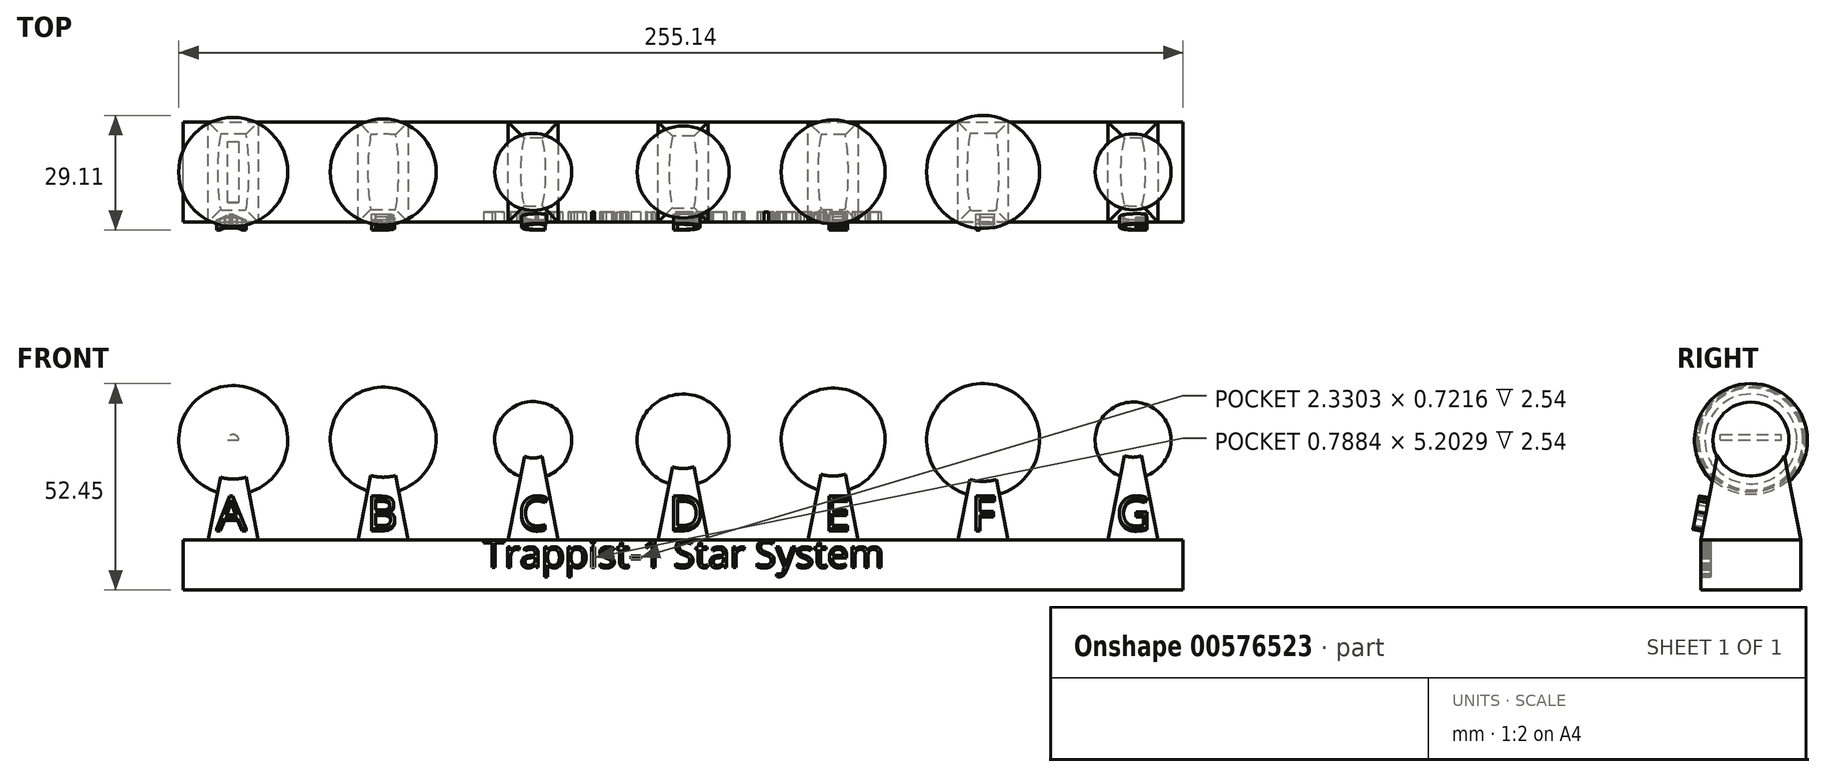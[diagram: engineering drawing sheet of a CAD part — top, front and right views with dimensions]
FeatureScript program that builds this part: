
annotation { "Feature Type Name" : "Feature", "Feature Type Description" : "" }
export const myFeature = defineFeature(function(context is Context, id is Id, definition is map)
    precondition{}
    {
        {
            var Q0;
            Q0=qCreatedBy(makeId("Front.planeOp"),FACE);
            var sketch = newSketch(context, id + "F0", { "sketchPlane" : qUnion([Q0])});
            skLineSegment(sketch, "E0.bottom", {"start": v(0, 0) * mm, "end": v(254, 0) * mm});
            skLineSegment(sketch, "E0.top", {"start": v(0, 12.7) * mm, "end": v(254, 12.7) * mm});
            skLineSegment(sketch, "E0.left", {"start": v(0, 0) * mm, "end": v(0, 12.7) * mm});
            skLineSegment(sketch, "E0.right", {"start": v(254, 0) * mm, "end": v(254, 12.7) * mm});
            skSolve(sketch);
        }
        {
            var Q0;
            Q0 = qSketchRegion(id + "F0", true);
            extrude(context, id + "F1", {"entities" : qUnion([Q0]), "depth" : 25.4 * mm, "offsetDistance" : 25.4 * mm});
        }
        {
            var Q0;
            Q0=makeQuery(id+"F1.opExtrude","SWEPT_FACE",FACE,{"disambiguationData":[OSD([sQuery(id+"F0.wireOp",EDGE,"E0.top")])]});
            var sketch = newSketch(context, id + "F2", { "sketchPlane" : qUnion([Q0])});
            skLineSegment(sketch, "E1.bottom", {"start": v(6.35, 0) * mm, "end": v(19.05, 0) * mm});
            skLineSegment(sketch, "E1.top", {"start": v(6.35, -25.4) * mm, "end": v(19.05, -25.4) * mm});
            skLineSegment(sketch, "E1.left", {"start": v(6.35, 0) * mm, "end": v(6.35, -25.4) * mm});
            skLineSegment(sketch, "E1.right", {"start": v(19.05, 0) * mm, "end": v(19.05, -25.4) * mm});
            skLineSegment(sketch, "E2.1.0.0", {"start": v(57.15, 0) * mm, "end": v(57.15, -25.4) * mm});
            skLineSegment(sketch, "E2.1.0.1", {"start": v(44.45, 0) * mm, "end": v(57.15, 0) * mm});
            skLineSegment(sketch, "E2.1.0.2", {"start": v(44.45, 0) * mm, "end": v(44.45, -25.4) * mm});
            skLineSegment(sketch, "E2.1.0.3", {"start": v(44.45, -25.4) * mm, "end": v(57.15, -25.4) * mm});
            skLineSegment(sketch, "E2.2.0.0", {"start": v(95.25, 0) * mm, "end": v(95.25, -25.4) * mm});
            skLineSegment(sketch, "E2.2.0.1", {"start": v(82.55, 0) * mm, "end": v(95.25, 0) * mm});
            skLineSegment(sketch, "E2.2.0.2", {"start": v(82.55, 0) * mm, "end": v(82.55, -25.4) * mm});
            skLineSegment(sketch, "E2.2.0.3", {"start": v(82.55, -25.4) * mm, "end": v(95.25, -25.4) * mm});
            skLineSegment(sketch, "E2.3.0.0", {"start": v(133.35, 0) * mm, "end": v(133.35, -25.4) * mm});
            skLineSegment(sketch, "E2.3.0.1", {"start": v(120.65, 0) * mm, "end": v(133.35, 0) * mm});
            skLineSegment(sketch, "E2.3.0.2", {"start": v(120.65, 0) * mm, "end": v(120.65, -25.4) * mm});
            skLineSegment(sketch, "E2.3.0.3", {"start": v(120.65, -25.4) * mm, "end": v(133.35, -25.4) * mm});
            skLineSegment(sketch, "E2.4.0.0", {"start": v(171.45, 0) * mm, "end": v(171.45, -25.4) * mm});
            skLineSegment(sketch, "E2.4.0.1", {"start": v(158.75, 0) * mm, "end": v(171.45, 0) * mm});
            skLineSegment(sketch, "E2.4.0.2", {"start": v(158.75, 0) * mm, "end": v(158.75, -25.4) * mm});
            skLineSegment(sketch, "E2.4.0.3", {"start": v(158.75, -25.4) * mm, "end": v(171.45, -25.4) * mm});
            skLineSegment(sketch, "E2.5.0.0", {"start": v(209.55, 0) * mm, "end": v(209.55, -25.4) * mm});
            skLineSegment(sketch, "E2.5.0.1", {"start": v(196.85, 0) * mm, "end": v(209.55, 0) * mm});
            skLineSegment(sketch, "E2.5.0.2", {"start": v(196.85, 0) * mm, "end": v(196.85, -25.4) * mm});
            skLineSegment(sketch, "E2.5.0.3", {"start": v(196.85, -25.4) * mm, "end": v(209.55, -25.4) * mm});
            skLineSegment(sketch, "E2.6.0.0", {"start": v(247.65, 0) * mm, "end": v(247.65, -25.4) * mm});
            skLineSegment(sketch, "E2.6.0.1", {"start": v(234.95, 0) * mm, "end": v(247.65, 0) * mm});
            skLineSegment(sketch, "E2.6.0.2", {"start": v(234.95, 0) * mm, "end": v(234.95, -25.4) * mm});
            skLineSegment(sketch, "E2.6.0.3", {"start": v(234.95, -25.4) * mm, "end": v(247.65, -25.4) * mm});
            skLineSegment(sketch, "E2.direction1", {"start": v(19.05, -25.4) * mm, "end": v(57.15, -25.4) * mm, "construction": true});
            skSolve(sketch);
        }
        {
            var Q0;
            Q0 = qSketchRegion(id + "F2", true);
            extrude(context, id + "F3", {"entities" : qUnion([Q0]), "operationType" : NewBodyOperationType.ADD, "depth" : 25.4 * mm, "offsetDistance" : 25.4 * mm, "hasDraft" : true, "draftAngle" : 11 * degree, "draftPullDirection" : true});
        }
        {
            var Q0;
            Q0=makeQuery(id+"F3.opExtrude","CAP_FACE",FACE,{"disambiguationData":[OSD([sQuery(id+"F2.wireOp",EDGE,"E1.bottom"),sQuery(id+"F2.wireOp",EDGE,"E1.top"),sQuery(id+"F2.wireOp",EDGE,"E1.left"),sQuery(id+"F2.wireOp",EDGE,"E1.right")])],"isStart":false});
            var sketch = newSketch(context, id + "F4", { "sketchPlane" : qUnion([Q0])});
            skLineSegment(sketch, "E3", {"start": v(12.7, -20.46) * mm, "end": v(12.7, -4.94) * mm});
            skLineSegment(sketch, "E4", {"start": v(12.7, -4.94) * mm, "end": v(12.7, 24.87) * mm});
            skLineSegment(sketch, "E5", {"start": v(12.7, 24.87) * mm, "end": v(12.7, -38.9) * mm});
            skCircle(sketch, "E6", {"center": v(12.7, -12.7) * mm, "radius": 13.84 * mm});
            skLineSegment(sketch, "E7", {"start": v(50.8, -20.46) * mm, "end": v(50.8, -4.94) * mm});
            skLineSegment(sketch, "E8.1.0.0", {"start": v(88.9, -20.46) * mm, "end": v(88.9, -4.94) * mm});
            skLineSegment(sketch, "E8.2.0.0", {"start": v(127, -20.46) * mm, "end": v(127, -4.94) * mm});
            skLineSegment(sketch, "E8.3.0.0", {"start": v(165.1, -20.46) * mm, "end": v(165.1, -4.94) * mm});
            skLineSegment(sketch, "E8.4.0.0", {"start": v(203.2, -20.46) * mm, "end": v(203.2, -4.94) * mm});
            skLineSegment(sketch, "E8.5.0.0", {"start": v(241.3, -20.46) * mm, "end": v(241.3, -4.94) * mm});
            skLineSegment(sketch, "E8.direction1", {"start": v(50.8, -20.46) * mm, "end": v(88.9, -20.46) * mm, "construction": true});
            skCircle(sketch, "E9", {"center": v(50.8, -12.7) * mm, "radius": 13.46 * mm});
            skCircle(sketch, "E10", {"center": v(88.9, -12.7) * mm, "radius": 9.78 * mm});
            skCircle(sketch, "E11", {"center": v(127, -12.7) * mm, "radius": 11.68 * mm});
            skCircle(sketch, "E12", {"center": v(165.1, -12.7) * mm, "radius": 13.2 * mm});
            skCircle(sketch, "E13", {"center": v(203.2, -12.7) * mm, "radius": 14.35 * mm});
            skCircle(sketch, "E14", {"center": v(241.3, -12.7) * mm, "radius": 9.65 * mm});
            skLineSegment(sketch, "E15", {"start": v(50.8, -4.94) * mm, "end": v(50.8, 11.68) * mm});
            skLineSegment(sketch, "E16", {"start": v(50.8, 11.68) * mm, "end": v(50.8, -38.95) * mm});
            skLineSegment(sketch, "E17", {"start": v(88.9, -4.94) * mm, "end": v(88.9, 14.66) * mm});
            skLineSegment(sketch, "E18", {"start": v(88.9, 14.66) * mm, "end": v(88.9, -43.53) * mm});
            skLineSegment(sketch, "E19", {"start": v(127, -4.94) * mm, "end": v(127, 8.7) * mm});
            skLineSegment(sketch, "E20", {"start": v(127, 8.7) * mm, "end": v(127, -40.55) * mm});
            skLineSegment(sketch, "E21", {"start": v(165.1, -4.94) * mm, "end": v(165.1, 10.77) * mm});
            skLineSegment(sketch, "E22", {"start": v(165.1, 10.77) * mm, "end": v(165.1, -40.78) * mm});
            skLineSegment(sketch, "E23", {"start": v(203.2, -4.94) * mm, "end": v(203.2, 10.5) * mm});
            skLineSegment(sketch, "E24", {"start": v(203.2, 10.5) * mm, "end": v(203.2, -36.48) * mm});
            skLineSegment(sketch, "E25", {"start": v(241.3, -4.94) * mm, "end": v(241.3, 4.89) * mm});
            skLineSegment(sketch, "E26", {"start": v(241.3, 4.89) * mm, "end": v(241.3, -30.18) * mm});
            skSolve(sketch);
        }
        {
            var Q0;
            {var subQ4=makeQuery(id+"F3.opExtrude","CAP_EDGE",EDGE,{"disambiguationData":[OSD([sQuery(id+"F2.wireOp",EDGE,"E1.right")])],"isStart":false});Q0=makeQuery(id+"F4.imprint","IMPRINT",FACE,{"disambiguationData":[TD([[makeQuery(id+"F4.imprint","IMPRINT",EDGE,{"derivedFrom":subQ4}),1.0]])]});}
            var Q1;
            Q1=sQuery(id+"F4.wireOp",EDGE,"E5");
            revolve(context, id + "F5", {"operationType" : NewBodyOperationType.ADD, "entities" : qUnion([Q0]), "axis" : qUnion([Q1]), "revolveType" : RevolveType.FULL});
        }
        {
            var Q0;
            {var subQ0=sQuery(id+"F4.wireOp",EDGE,"E16");var subQ4=makeQuery(id+"F4.imprint","IMPRINT",VERTEX,{"derivedFrom":subQ0});Q0=makeQuery(id+"F4.imprint","IMPRINT",FACE,{"disambiguationData":[TD([[makeQuery(id+"F4.imprint","IMPRINT",EDGE,{"disambiguationData":[TD([[subQ4,1.0]])],"derivedFrom":subQ0}),1.0]])]});}
            var Q1;
            Q1=sQuery(id+"F4.wireOp",EDGE,"E16");
            revolve(context, id + "F6", {"operationType" : NewBodyOperationType.ADD, "entities" : qUnion([Q0]), "axis" : qUnion([Q1]), "revolveType" : RevolveType.FULL});
        }
        {
            var Q0;
            {var subQ0=sQuery(id+"F4.wireOp",EDGE,"E18");var subQ4=makeQuery(id+"F4.imprint","IMPRINT",VERTEX,{"derivedFrom":subQ0});Q0=makeQuery(id+"F4.imprint","IMPRINT",FACE,{"disambiguationData":[TD([[makeQuery(id+"F4.imprint","IMPRINT",EDGE,{"disambiguationData":[TD([[subQ4,1.0]])],"derivedFrom":subQ0}),1.0]])]});}
            var Q1;
            Q1=sQuery(id+"F4.wireOp",EDGE,"E17");
            revolve(context, id + "F7", {"operationType" : NewBodyOperationType.ADD, "entities" : qUnion([Q0]), "axis" : qUnion([Q1]), "revolveType" : RevolveType.FULL});
        }
        {
            var Q0;
            {var subQ0=sQuery(id+"F4.wireOp",EDGE,"E20");var subQ4=makeQuery(id+"F4.imprint","IMPRINT",VERTEX,{"derivedFrom":subQ0});Q0=makeQuery(id+"F4.imprint","IMPRINT",FACE,{"disambiguationData":[TD([[makeQuery(id+"F4.imprint","IMPRINT",EDGE,{"disambiguationData":[TD([[subQ4,1.0]])],"derivedFrom":subQ0}),1.0]])]});}
            var Q1;
            Q1=sQuery(id+"F4.wireOp",EDGE,"E20");
            revolve(context, id + "F8", {"operationType" : NewBodyOperationType.ADD, "entities" : qUnion([Q0]), "axis" : qUnion([Q1]), "revolveType" : RevolveType.FULL});
        }
        {
            var Q0;
            {var subQ0=sQuery(id+"F4.wireOp",EDGE,"E22");var subQ4=makeQuery(id+"F4.imprint","IMPRINT",VERTEX,{"derivedFrom":subQ0});Q0=makeQuery(id+"F4.imprint","IMPRINT",FACE,{"disambiguationData":[TD([[makeQuery(id+"F4.imprint","IMPRINT",EDGE,{"disambiguationData":[TD([[subQ4,1.0]])],"derivedFrom":subQ0}),1.0]])]});}
            var Q1;
            Q1=sQuery(id+"F4.wireOp",EDGE,"E22");
            revolve(context, id + "F9", {"operationType" : NewBodyOperationType.ADD, "entities" : qUnion([Q0]), "axis" : qUnion([Q1]), "revolveType" : RevolveType.FULL});
        }
        {
            var Q0;
            {var subQ0=sQuery(id+"F4.wireOp",EDGE,"E24");var subQ4=makeQuery(id+"F4.imprint","IMPRINT",VERTEX,{"derivedFrom":subQ0});Q0=makeQuery(id+"F4.imprint","IMPRINT",FACE,{"disambiguationData":[TD([[makeQuery(id+"F4.imprint","IMPRINT",EDGE,{"disambiguationData":[TD([[subQ4,1.0]])],"derivedFrom":subQ0}),1.0]])]});}
            var Q1;
            Q1=sQuery(id+"F4.wireOp",EDGE,"E24");
            revolve(context, id + "F10", {"operationType" : NewBodyOperationType.ADD, "entities" : qUnion([Q0]), "axis" : qUnion([Q1]), "revolveType" : RevolveType.FULL});
        }
        {
            var Q0;
            {var subQ0=sQuery(id+"F4.wireOp",EDGE,"E26");var subQ4=makeQuery(id+"F4.imprint","IMPRINT",VERTEX,{"derivedFrom":subQ0});Q0=makeQuery(id+"F4.imprint","IMPRINT",FACE,{"disambiguationData":[TD([[makeQuery(id+"F4.imprint","IMPRINT",EDGE,{"disambiguationData":[TD([[subQ4,1.0]])],"derivedFrom":subQ0}),1.0]])]});}
            var Q1;
            Q1=sQuery(id+"F4.wireOp",EDGE,"E26");
            revolve(context, id + "F11", {"operationType" : NewBodyOperationType.ADD, "entities" : qUnion([Q0]), "axis" : qUnion([Q1]), "revolveType" : RevolveType.FULL});
        }
        {
            var Q0;
            Q0=makeQuery(id+"F1.opExtrude","CAP_FACE",FACE,{"disambiguationData":[OSD([sQuery(id+"F0.wireOp",EDGE,"E0.bottom"),sQuery(id+"F0.wireOp",EDGE,"E0.top"),sQuery(id+"F0.wireOp",EDGE,"E0.left"),sQuery(id+"F0.wireOp",EDGE,"E0.right")])],"isStart":false});
            var sketch = newSketch(context, id + "F12", { "sketchPlane" : qUnion([Q0])});
            skText(sketch, "E27", { "text": "Trappist-1 Star System\n", "fontName": "OpenSans-Regular.ttf"});
            const initialGuessF12  = {"E27": [0.0762, 0.0057, 1, 0, 0.007]};
            skSetInitialGuess(sketch, initialGuessF12);
            skSolve(sketch);
        }
        {
            var Q0;
            Q0 = qSketchRegion(id + "F12", true);
            extrude(context, id + "F13", {"entities" : qUnion([Q0]), "operationType" : NewBodyOperationType.REMOVE, "oppositeDirection" : true, "depth" : 2.54 * mm, "offsetDistance" : 25.4 * mm});
        }
        {
            var Q0;
            Q0=makeQuery(id+"F3.opExtrude","SWEPT_FACE",FACE,{"disambiguationData":[OSD([sQuery(id+"F2.wireOp",EDGE,"E1.top")])]});
            var sketch = newSketch(context, id + "F14", { "sketchPlane" : qUnion([Q0])});
            skText(sketch, "E28", { "text": "A          B          C          D          E          F          G", "fontName": "OpenSans-Regular.ttf"});
            const initialGuessF14  = {"E28": [0.00843, 0.01002, 1, 0, 0.00853]};
            skSetInitialGuess(sketch, initialGuessF14);
            skSolve(sketch);
        }
        {
            var Q0;
            Q0 = qSketchRegion(id + "F14", true);
            extrude(context, id + "F15", {"entities" : qUnion([Q0]), "operationType" : NewBodyOperationType.ADD, "depth" : 2.54 * mm, "offsetDistance" : 25.4 * mm});
        }
    });
